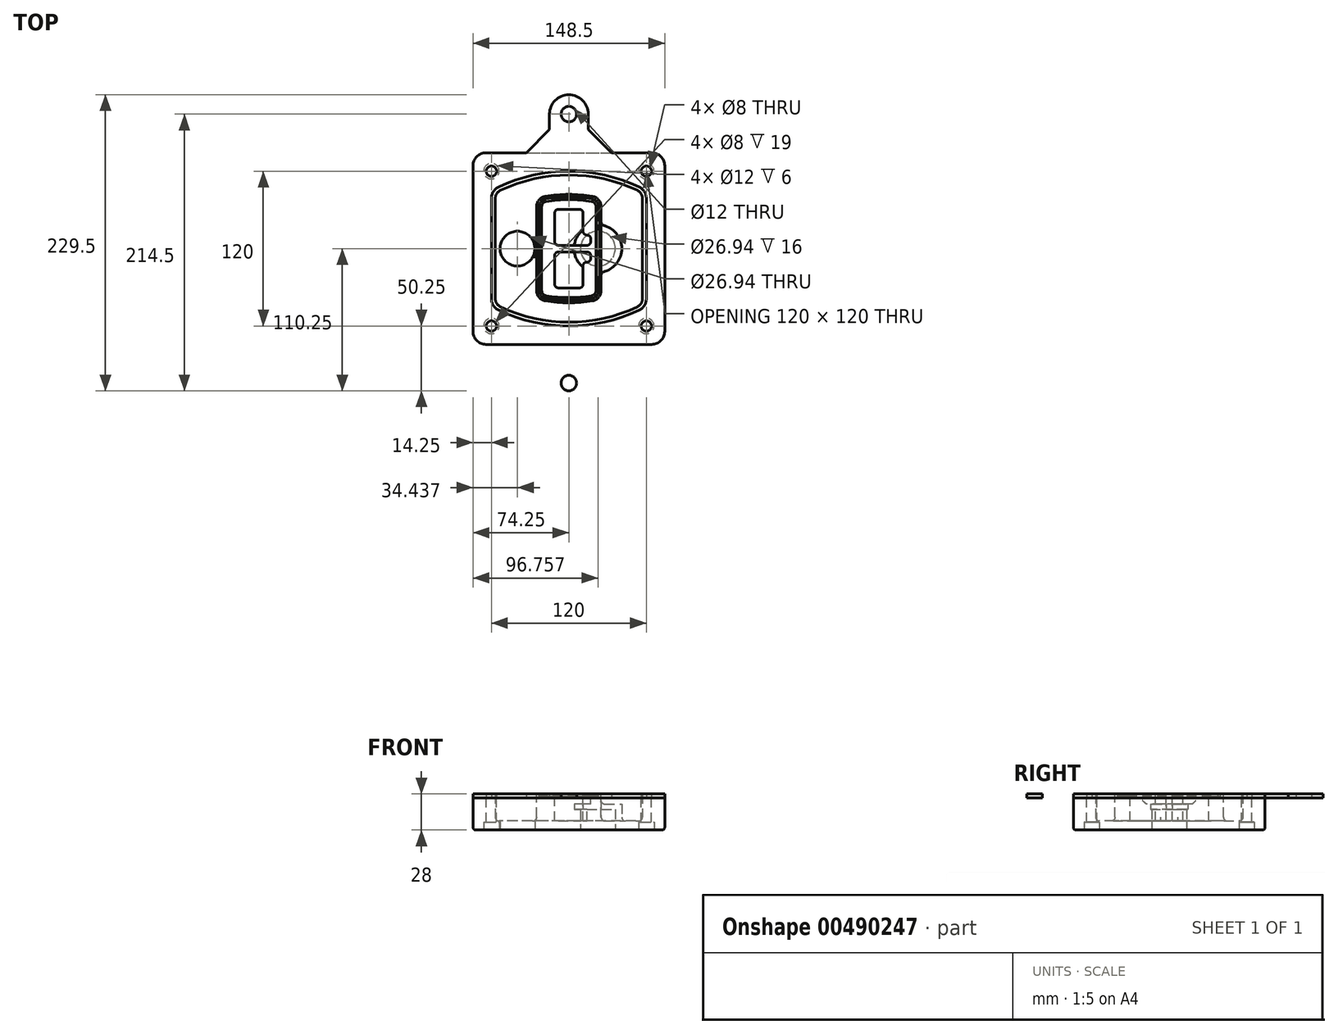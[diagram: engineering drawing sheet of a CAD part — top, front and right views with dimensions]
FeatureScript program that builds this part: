
annotation { "Feature Type Name" : "Feature", "Feature Type Description" : "" }
export const myFeature = defineFeature(function(context is Context, id is Id, definition is map)
    precondition{}
    {
        {
            var Q0;
            Q0=qCreatedBy(makeId("Top.planeOp"),FACE);
            var sketch = newSketch(context, id + "F0", { "sketchPlane" : qUnion([Q0])});
            skPoint(sketch, "E0.rect.middle", {"position": v(0, 0) * mm});
            skLineSegment(sketch, "E1.bottom", {"start": v(-64.25, -74.25) * mm, "end": v(64.25, -74.25) * mm});
            skLineSegment(sketch, "E1.top", {"start": v(-64.25, 74.25) * mm, "end": v(64.25, 74.25) * mm});
            skLineSegment(sketch, "E1.left", {"start": v(-74.25, -64.25) * mm, "end": v(-74.25, 64.25) * mm});
            skLineSegment(sketch, "E1.right", {"start": v(74.25, -64.25) * mm, "end": v(74.25, 64.25) * mm});
            skLineSegment(sketch, "E2", {"start": v(-74.25, 74.25) * mm, "end": v(74.25, -74.25) * mm, "construction": true});
            skLineSegment(sketch, "E3", {"start": v(74.25, 74.25) * mm, "end": v(-74.25, -74.25) * mm, "construction": true});
            skCircle(sketch, "E4", {"center": v(-60, 60) * mm, "radius": 4 * mm});
            skCircle(sketch, "E5", {"center": v(60, 60) * mm, "radius": 4 * mm});
            skCircle(sketch, "E6", {"center": v(60, -60) * mm, "radius": 4 * mm});
            skCircle(sketch, "E7", {"center": v(-60, -60) * mm, "radius": 4 * mm});
            skLineSegment(sketch, "E8", {"start": v(-60, 60) * mm, "end": v(60, 60) * mm, "construction": true});
            skLineSegment(sketch, "E9", {"start": v(60, 60) * mm, "end": v(60, -60) * mm, "construction": true});
            skLineSegment(sketch, "E10", {"start": v(60, -60) * mm, "end": v(-60, -60) * mm, "construction": true});
            skLineSegment(sketch, "E11", {"start": v(-60, -60) * mm, "end": v(-60, 60) * mm, "construction": true});
            skLineSegment(sketch, "E12", {"start": v(-60, 38.83) * mm, "end": v(-60, -38.83) * mm});
            skLineSegment(sketch, "E13", {"start": v(60, 38.83) * mm, "end": v(60, -38.83) * mm});
            skArc(sketch, "E14", {"start": v(54.26, 47.88) * mm, "mid": v(0, 60) * mm, "end": v(-54.26, 47.88) * mm});
            skArc(sketch, "E15", {"start": v(-54.26, -47.88) * mm, "mid": v(0, -60) * mm, "end": v(54.26, -47.88) * mm});
            skLineSegment(sketch, "E16", {"start": v(-60, 0) * mm, "end": v(60, 0) * mm, "construction": true});
            skPoint(sketch, "E17.visualSharp", {"position": v(-60, -45) * mm});
            skArc(sketch, "E17.filletArc", {"start": v(-60, -38.83) * mm, "mid": v(-58.44, -44.2) * mm, "end": v(-54.26, -47.88) * mm});
            skPoint(sketch, "E18.visualSharp", {"position": v(-60, 45) * mm});
            skArc(sketch, "E18.filletArc", {"start": v(-54.26, 47.88) * mm, "mid": v(-58.44, 44.2) * mm, "end": v(-60, 38.83) * mm});
            skPoint(sketch, "E19.visualSharp", {"position": v(60, 45) * mm});
            skArc(sketch, "E19.filletArc", {"start": v(60, 38.83) * mm, "mid": v(58.44, 44.2) * mm, "end": v(54.26, 47.88) * mm});
            skPoint(sketch, "E20.visualSharp", {"position": v(60, -45) * mm});
            skArc(sketch, "E20.filletArc", {"start": v(54.26, -47.88) * mm, "mid": v(58.44, -44.2) * mm, "end": v(60, -38.83) * mm});
            skPoint(sketch, "E21.visualSharp", {"position": v(-74.25, 74.25) * mm});
            skArc(sketch, "E21.filletArc", {"start": v(-64.25, 74.25) * mm, "mid": v(-71.32, 71.32) * mm, "end": v(-74.25, 64.25) * mm});
            skPoint(sketch, "E22.visualSharp", {"position": v(74.25, 74.25) * mm});
            skArc(sketch, "E22.filletArc", {"start": v(74.25, 64.25) * mm, "mid": v(71.32, 71.32) * mm, "end": v(64.25, 74.25) * mm});
            skPoint(sketch, "E23.visualSharp", {"position": v(74.25, -74.25) * mm});
            skArc(sketch, "E23.filletArc", {"start": v(64.25, -74.25) * mm, "mid": v(71.32, -71.32) * mm, "end": v(74.25, -64.25) * mm});
            skPoint(sketch, "E24.visualSharp", {"position": v(-74.25, -74.25) * mm});
            skArc(sketch, "E24.filletArc", {"start": v(-74.25, -64.25) * mm, "mid": v(-71.32, -71.32) * mm, "end": v(-64.25, -74.25) * mm});
            skArc(sketch, "E25.0", {"start": v(57, 38.83) * mm, "mid": v(55.9, 42.58) * mm, "end": v(52.98, 45.17) * mm});
            skLineSegment(sketch, "E25.1", {"start": v(57, 38.83) * mm, "end": v(57, -38.83) * mm});
            skArc(sketch, "E25.2", {"start": v(52.98, -45.17) * mm, "mid": v(55.9, -42.58) * mm, "end": v(57, -38.83) * mm});
            skArc(sketch, "E25.3", {"start": v(-52.98, -45.17) * mm, "mid": v(0, -57) * mm, "end": v(52.98, -45.17) * mm});
            skArc(sketch, "E25.4", {"start": v(-57, -38.83) * mm, "mid": v(-55.9, -42.58) * mm, "end": v(-52.98, -45.17) * mm});
            skArc(sketch, "E25.5", {"start": v(52.98, 45.17) * mm, "mid": v(0, 57) * mm, "end": v(-52.98, 45.17) * mm});
            skLineSegment(sketch, "E25.6", {"start": v(-57, 38.83) * mm, "end": v(-57, -38.83) * mm});
            skArc(sketch, "E25.7", {"start": v(-52.98, 45.17) * mm, "mid": v(-55.9, 42.58) * mm, "end": v(-57, 38.83) * mm});
            skArc(sketch, "E26.0", {"start": v(-55.96, 51.5) * mm, "mid": v(-61.82, 46.33) * mm, "end": v(-64, 38.83) * mm});
            skArc(sketch, "E26.1", {"start": v(55.96, 51.5) * mm, "mid": v(0, 64) * mm, "end": v(-55.96, 51.5) * mm});
            skArc(sketch, "E26.2", {"start": v(64, 38.83) * mm, "mid": v(61.82, 46.33) * mm, "end": v(55.96, 51.5) * mm});
            skLineSegment(sketch, "E26.3", {"start": v(64, 38.83) * mm, "end": v(64, -38.83) * mm});
            skArc(sketch, "E26.4", {"start": v(55.96, -51.5) * mm, "mid": v(61.82, -46.33) * mm, "end": v(64, -38.83) * mm});
            skLineSegment(sketch, "E26.5", {"start": v(-64, 38.83) * mm, "end": v(-64, -38.83) * mm});
            skArc(sketch, "E26.6", {"start": v(-55.96, -51.5) * mm, "mid": v(0, -64) * mm, "end": v(55.96, -51.5) * mm});
            skArc(sketch, "E26.7", {"start": v(-64, -38.83) * mm, "mid": v(-61.82, -46.33) * mm, "end": v(-55.96, -51.5) * mm});
            skSolve(sketch);
        }
        {
            var Q0;
            Q0=makeQuery(id+"F0.imprint","IMPRINT",FACE,{"disambiguationData":[TD([[makeQuery(id+"F0.imprint","IMPRINT",EDGE,{"derivedFrom":sQuery(id+"F0.wireOp",EDGE,"E1.bottom")}),1.0]])]});
            var Q1;
            Q1=makeQuery(id+"F0.imprint","IMPRINT",FACE,{"disambiguationData":[TD([[makeQuery(id+"F0.imprint","IMPRINT",EDGE,{"derivedFrom":sQuery(id+"F0.wireOp",EDGE,"E12")}),1.0]])]});
            var Q2;
            Q2=makeQuery(id+"F0.imprint","IMPRINT",FACE,{"disambiguationData":[TD([[makeQuery(id+"F0.imprint","IMPRINT",EDGE,{"derivedFrom":sQuery(id+"F0.wireOp",EDGE,"E25.0")}),1.0]])]});
            var Q3;
            Q3=makeQuery(id+"F0.imprint","IMPRINT",FACE,{"disambiguationData":[TD([[makeQuery(id+"F0.imprint","IMPRINT",EDGE,{"derivedFrom":sQuery(id+"F0.wireOp",EDGE,"E12")}),-1.0]])]});
            extrude(context, id + "F1", {"entities" : qUnion([Q0, Q1, Q2, Q3]), "oppositeDirection" : true, "depth" : 25 * mm});
        }
        {
            var Q0;
            Q0=makeQuery(id+"F0.imprint","IMPRINT",FACE,{"disambiguationData":[TD([[makeQuery(id+"F0.imprint","IMPRINT",EDGE,{"derivedFrom":sQuery(id+"F0.wireOp",EDGE,"E12")}),1.0]])]});
            extrude(context, id + "F2", {"entities" : qUnion([Q0]), "operationType" : NewBodyOperationType.ADD, "depth" : 3 * mm});
        }
        {
            var Q0;
            Q0=makeQuery(id+"F0.imprint","IMPRINT",FACE,{"disambiguationData":[TD([[makeQuery(id+"F0.imprint","IMPRINT",EDGE,{"derivedFrom":sQuery(id+"F0.wireOp",EDGE,"E25.0")}),1.0]])]});
            extrude(context, id + "F3", {"entities" : qUnion([Q0]), "operationType" : NewBodyOperationType.REMOVE, "oppositeDirection" : true, "depth" : 18 * mm});
        }
        {
            var Q0;
            Q0=makeQuery(id+"F2.opExtrude","CAP_FACE",FACE,{"disambiguationData":[OSD([sQuery(id+"F0.wireOp",EDGE,"E12"),sQuery(id+"F0.wireOp",EDGE,"E13"),sQuery(id+"F0.wireOp",EDGE,"E14"),sQuery(id+"F0.wireOp",EDGE,"E15"),sQuery(id+"F0.wireOp",EDGE,"E17.filletArc"),sQuery(id+"F0.wireOp",EDGE,"E18.filletArc"),sQuery(id+"F0.wireOp",EDGE,"E19.filletArc"),sQuery(id+"F0.wireOp",EDGE,"E20.filletArc"),sQuery(id+"F0.wireOp",EDGE,"E25.0"),sQuery(id+"F0.wireOp",EDGE,"E25.1"),sQuery(id+"F0.wireOp",EDGE,"E25.2"),sQuery(id+"F0.wireOp",EDGE,"E25.3"),sQuery(id+"F0.wireOp",EDGE,"E25.4"),sQuery(id+"F0.wireOp",EDGE,"E25.5"),sQuery(id+"F0.wireOp",EDGE,"E25.6"),sQuery(id+"F0.wireOp",EDGE,"E25.7")])],"isStart":false});
            var sketch = newSketch(context, id + "F4", { "sketchPlane" : qUnion([Q0])});
            skArc(sketch, "E27.0", {"start": v(-18.34, -40.45) * mm, "mid": v(0, -42) * mm, "end": v(18.34, -40.45) * mm});
            skArc(sketch, "E28.0", {"start": v(18.34, 40.45) * mm, "mid": v(0, 42) * mm, "end": v(-18.34, 40.45) * mm});
            skLineSegment(sketch, "E29", {"start": v(-25, 32.57) * mm, "end": v(-25, -32.57) * mm});
            skLineSegment(sketch, "E30", {"start": v(25, 32.57) * mm, "end": v(25, -32.57) * mm});
            skLineSegment(sketch, "E31", {"start": v(-25, 39.1) * mm, "end": v(25, 39.1) * mm, "construction": true});
            skLineSegment(sketch, "E32", {"start": v(-25, -39.1) * mm, "end": v(25, -39.1) * mm, "construction": true});
            skPoint(sketch, "E33.visualSharp", {"position": v(-25, 39.1) * mm});
            skArc(sketch, "E33.filletArc", {"start": v(-18.34, 40.45) * mm, "mid": v(-23.11, 37.73) * mm, "end": v(-25, 32.57) * mm});
            skPoint(sketch, "E34.visualSharp", {"position": v(25, 39.1) * mm});
            skArc(sketch, "E34.filletArc", {"start": v(25, 32.57) * mm, "mid": v(23.11, 37.73) * mm, "end": v(18.34, 40.45) * mm});
            skPoint(sketch, "E35.visualSharp", {"position": v(25, -39.1) * mm});
            skArc(sketch, "E35.filletArc", {"start": v(18.34, -40.45) * mm, "mid": v(23.11, -37.73) * mm, "end": v(25, -32.57) * mm});
            skPoint(sketch, "E36.visualSharp", {"position": v(-25, -39.1) * mm});
            skArc(sketch, "E36.filletArc", {"start": v(-25, -32.57) * mm, "mid": v(-23.11, -37.73) * mm, "end": v(-18.34, -40.45) * mm});
            skArc(sketch, "E37.0", {"start": v(52.98, 45.17) * mm, "mid": v(0, 57) * mm, "end": v(-52.98, 45.17) * mm});
            skArc(sketch, "E37.1", {"start": v(-52.98, 45.17) * mm, "mid": v(-55.9, 42.58) * mm, "end": v(-57, 38.83) * mm});
            skLineSegment(sketch, "E37.2", {"start": v(-57, 38.83) * mm, "end": v(-57, -38.83) * mm});
            skArc(sketch, "E37.3", {"start": v(-57, -38.83) * mm, "mid": v(-55.9, -42.58) * mm, "end": v(-52.98, -45.17) * mm});
            skArc(sketch, "E37.4", {"start": v(-52.98, -45.17) * mm, "mid": v(0, -57) * mm, "end": v(52.98, -45.17) * mm});
            skArc(sketch, "E37.5", {"start": v(52.98, -45.17) * mm, "mid": v(55.9, -42.58) * mm, "end": v(57, -38.83) * mm});
            skLineSegment(sketch, "E37.6", {"start": v(57, 38.83) * mm, "end": v(57, -38.83) * mm});
            skArc(sketch, "E37.7", {"start": v(57, 38.83) * mm, "mid": v(55.9, 42.58) * mm, "end": v(52.98, 45.17) * mm});
            skLineSegment(sketch, "E38.0", {"start": v(23, 32.57) * mm, "end": v(23, -32.57) * mm});
            skArc(sketch, "E38.1", {"start": v(18, -38.48) * mm, "mid": v(21.58, -36.44) * mm, "end": v(23, -32.57) * mm});
            skArc(sketch, "E38.2", {"start": v(-18, -38.48) * mm, "mid": v(0, -40) * mm, "end": v(18, -38.48) * mm});
            skArc(sketch, "E38.3", {"start": v(-23, -32.57) * mm, "mid": v(-21.58, -36.44) * mm, "end": v(-18, -38.48) * mm});
            skLineSegment(sketch, "E38.4", {"start": v(-23, 32.57) * mm, "end": v(-23, -32.57) * mm});
            skArc(sketch, "E38.5", {"start": v(23, 32.57) * mm, "mid": v(21.58, 36.44) * mm, "end": v(18, 38.48) * mm});
            skArc(sketch, "E38.6", {"start": v(-18, 38.48) * mm, "mid": v(-21.58, 36.44) * mm, "end": v(-23, 32.57) * mm});
            skArc(sketch, "E38.7", {"start": v(18, 38.48) * mm, "mid": v(0, 40) * mm, "end": v(-18, 38.48) * mm});
            skArc(sketch, "E39.0", {"start": v(21, 32.57) * mm, "mid": v(20.06, 35.15) * mm, "end": v(17.67, 36.5) * mm});
            skLineSegment(sketch, "E39.1", {"start": v(21, 32.57) * mm, "end": v(21, -32.57) * mm});
            skArc(sketch, "E39.2", {"start": v(17.67, -36.5) * mm, "mid": v(20.06, -35.15) * mm, "end": v(21, -32.57) * mm});
            skArc(sketch, "E39.3", {"start": v(-17.67, -36.5) * mm, "mid": v(0, -38) * mm, "end": v(17.67, -36.5) * mm});
            skArc(sketch, "E39.4", {"start": v(-21, -32.57) * mm, "mid": v(-20.06, -35.15) * mm, "end": v(-17.67, -36.5) * mm});
            skArc(sketch, "E39.5", {"start": v(17.67, 36.5) * mm, "mid": v(0, 38) * mm, "end": v(-17.67, 36.5) * mm});
            skLineSegment(sketch, "E39.6", {"start": v(-21, 32.57) * mm, "end": v(-21, -32.57) * mm});
            skArc(sketch, "E39.7", {"start": v(-17.67, 36.5) * mm, "mid": v(-20.06, 35.15) * mm, "end": v(-21, 32.57) * mm});
            skLineSegment(sketch, "E40", {"start": v(-25, 0) * mm, "end": v(25, 0) * mm, "construction": true});
            skLineSegment(sketch, "E41", {"start": v(-11, 5.5) * mm, "end": v(-11, 27.5) * mm});
            skLineSegment(sketch, "E42", {"start": v(-8, 30.5) * mm, "end": v(8, 30.5) * mm});
            skLineSegment(sketch, "E43", {"start": v(11, 27.5) * mm, "end": v(11, 13.5) * mm});
            skLineSegment(sketch, "E44", {"start": v(14, 10.5) * mm, "end": v(14, 10.5) * mm});
            skLineSegment(sketch, "E45", {"start": v(17, 7.5) * mm, "end": v(17, 5.5) * mm});
            skLineSegment(sketch, "E46", {"start": v(14, 2.5) * mm, "end": v(-8, 2.5) * mm});
            skPoint(sketch, "E47.visualSharp", {"position": v(-11, 30.5) * mm});
            skArc(sketch, "E47.filletArc", {"start": v(-8, 30.5) * mm, "mid": v(-10.12, 29.62) * mm, "end": v(-11, 27.5) * mm});
            skPoint(sketch, "E48.visualSharp", {"position": v(11, 30.5) * mm});
            skArc(sketch, "E48.filletArc", {"start": v(11, 27.5) * mm, "mid": v(10.12, 29.62) * mm, "end": v(8, 30.5) * mm});
            skPoint(sketch, "E49.visualSharp", {"position": v(11, 10.5) * mm});
            skArc(sketch, "E49.filletArc", {"start": v(11, 13.5) * mm, "mid": v(11.88, 11.38) * mm, "end": v(14, 10.5) * mm});
            skPoint(sketch, "E50.visualSharp", {"position": v(17, 10.5) * mm});
            skArc(sketch, "E50.filletArc", {"start": v(17, 7.5) * mm, "mid": v(16.12, 9.62) * mm, "end": v(14, 10.5) * mm});
            skPoint(sketch, "E51.visualSharp", {"position": v(17, 2.5) * mm});
            skArc(sketch, "E51.filletArc", {"start": v(14, 2.5) * mm, "mid": v(16.12, 3.38) * mm, "end": v(17, 5.5) * mm});
            skPoint(sketch, "E52.visualSharp", {"position": v(-11, 2.5) * mm});
            skArc(sketch, "E52.filletArc", {"start": v(-11, 5.5) * mm, "mid": v(-10.12, 3.38) * mm, "end": v(-8, 2.5) * mm});
            skLineSegment(sketch, "E53.0.MirrorCS", {"start": v(14, -2.5) * mm, "end": v(-8, -2.5) * mm});
            skArc(sketch, "E54.0.MirrorCS", {"start": v(-11, -5.5) * mm, "mid": v(-10.12, -3.38) * mm, "end": v(-8, -2.5) * mm});
            skLineSegment(sketch, "E55.0.MirrorCS", {"start": v(-11, -5.5) * mm, "end": v(-11, -27.5) * mm});
            skArc(sketch, "E56.0.MirrorCS", {"start": v(-8, -30.5) * mm, "mid": v(-10.12, -29.62) * mm, "end": v(-11, -27.5) * mm});
            skLineSegment(sketch, "E57.0.MirrorCS", {"start": v(-8, -30.5) * mm, "end": v(8, -30.5) * mm});
            skArc(sketch, "E58.0.MirrorCS", {"start": v(11, -27.5) * mm, "mid": v(10.12, -29.62) * mm, "end": v(8, -30.5) * mm});
            skLineSegment(sketch, "E59.0.MirrorCS", {"start": v(11, -27.5) * mm, "end": v(11, -13.5) * mm});
            skArc(sketch, "E60.0.MirrorCS", {"start": v(11, -13.5) * mm, "mid": v(11.88, -11.38) * mm, "end": v(14, -10.5) * mm});
            skArc(sketch, "E61.0.MirrorCS", {"start": v(17, -7.5) * mm, "mid": v(16.12, -9.62) * mm, "end": v(14, -10.5) * mm});
            skLineSegment(sketch, "E62.0.MirrorCS", {"start": v(17, -7.5) * mm, "end": v(17, -5.5) * mm});
            skArc(sketch, "E63.0.MirrorCS", {"start": v(14, -2.5) * mm, "mid": v(16.12, -3.38) * mm, "end": v(17, -5.5) * mm});
            skSolve(sketch);
        }
        {
            var Q0;
            Q0=makeQuery(id+"F4.imprint","IMPRINT",FACE,{"disambiguationData":[TD([[makeQuery(id+"F4.imprint","IMPRINT",EDGE,{"derivedFrom":sQuery(id+"F4.wireOp",EDGE,"E27.0")}),1.0]])]});
            var Q1;
            Q1=makeQuery(id+"F4.imprint","IMPRINT",FACE,{"disambiguationData":[TD([[makeQuery(id+"F4.imprint","IMPRINT",EDGE,{"derivedFrom":sQuery(id+"F4.wireOp",EDGE,"E38.0")}),-1.0]])]});
            var Q2;
            Q2=makeQuery(id+"F4.imprint","IMPRINT",FACE,{"disambiguationData":[TD([[makeQuery(id+"F4.imprint","IMPRINT",EDGE,{"derivedFrom":sQuery(id+"F4.wireOp",EDGE,"E39.0")}),1.0]])]});
            extrude(context, id + "F5", {"entities" : qUnion([Q0, Q1, Q2]), "operationType" : NewBodyOperationType.ADD, "endBound" : BoundingType.UP_TO_NEXT, "oppositeDirection" : true, "depth" : 25 * mm});
        }
        {
            var Q0;
            Q0=makeQuery(id+"F4.imprint","IMPRINT",FACE,{"disambiguationData":[TD([[makeQuery(id+"F4.imprint","IMPRINT",EDGE,{"derivedFrom":sQuery(id+"F4.wireOp",EDGE,"E38.0")}),-1.0]])]});
            extrude(context, id + "F6", {"entities" : qUnion([Q0]), "operationType" : NewBodyOperationType.REMOVE, "oppositeDirection" : true, "depth" : 2 * mm});
        }
        {
            var Q0;
            Q0=makeQuery(id+"F1.opExtrude","CAP_FACE",FACE,{"disambiguationData":[OSD([sQuery(id+"F0.wireOp",EDGE,"E1.bottom"),sQuery(id+"F0.wireOp",EDGE,"E1.top"),sQuery(id+"F0.wireOp",EDGE,"E1.left"),sQuery(id+"F0.wireOp",EDGE,"E1.right"),sQuery(id+"F0.wireOp",EDGE,"E4"),sQuery(id+"F0.wireOp",EDGE,"E5"),sQuery(id+"F0.wireOp",EDGE,"E6"),sQuery(id+"F0.wireOp",EDGE,"E7"),sQuery(id+"F0.wireOp",EDGE,"E21.filletArc"),sQuery(id+"F0.wireOp",EDGE,"E22.filletArc"),sQuery(id+"F0.wireOp",EDGE,"E23.filletArc"),sQuery(id+"F0.wireOp",EDGE,"E24.filletArc")])],"isStart":false});
            var sketch = newSketch(context, id + "F7", { "sketchPlane" : qUnion([Q0])});
            skCircle(sketch, "E64", {"center": v(22.5, 0) * mm, "radius": 13.47 * mm});
            skCircle(sketch, "E65", {"center": v(-39.81, 0) * mm, "radius": 13.47 * mm});
            skLineSegment(sketch, "E66", {"start": v(74.25, 0) * mm, "end": v(-74.25, 0) * mm});
            skCircle(sketch, "E67", {"center": v(22.5, 0) * mm, "radius": 18.47 * mm});
            skCircle(sketch, "E68", {"center": v(60, -60) * mm, "radius": 6 * mm});
            skCircle(sketch, "E69", {"center": v(-60, -60) * mm, "radius": 6 * mm});
            skCircle(sketch, "E70", {"center": v(-60, 60) * mm, "radius": 6 * mm});
            skCircle(sketch, "E71", {"center": v(60, 60) * mm, "radius": 6 * mm});
            skSolve(sketch);
        }
        {
            var Q0;
            {var subQ1=sQuery(id+"F7.wireOp",EDGE,"E66");var subQ4=sQuery(id+"F7.wireOp",EDGE,"E64");var subQ6=makeQuery(id+"F7.imprint","INTERSECT",VERTEX,{"disambiguationData":[OD(0.0)],"derivedFrom":[subQ4,subQ1]});Q0=makeQuery(id+"F7.imprint","IMPRINT",FACE,{"disambiguationData":[TD([[makeQuery(id+"F7.imprint","IMPRINT",EDGE,{"disambiguationData":[TD([[subQ6,-1.0]])],"derivedFrom":subQ4}),-1.0]])]});}
            var Q1;
            {var subQ0=sQuery(id+"F7.wireOp",EDGE,"E66");var subQ1=sQuery(id+"F7.wireOp",EDGE,"E64");var subQ3=makeQuery(id+"F7.imprint","INTERSECT",VERTEX,{"disambiguationData":[OD(0.0)],"derivedFrom":[subQ1,subQ0]});Q1=makeQuery(id+"F7.imprint","IMPRINT",FACE,{"disambiguationData":[TD([[makeQuery(id+"F7.imprint","IMPRINT",EDGE,{"disambiguationData":[TD([[subQ3,-1.0]])],"derivedFrom":subQ1}),1.0]])]});}
            var Q2;
            {var subQ0=sQuery(id+"F7.wireOp",EDGE,"E66");var subQ1=sQuery(id+"F7.wireOp",EDGE,"E64");var subQ3=makeQuery(id+"F7.imprint","INTERSECT",VERTEX,{"disambiguationData":[OD(0.0)],"derivedFrom":[subQ1,subQ0]});Q2=makeQuery(id+"F7.imprint","IMPRINT",FACE,{"disambiguationData":[TD([[makeQuery(id+"F7.imprint","IMPRINT",EDGE,{"disambiguationData":[TD([[subQ3,1.0]])],"derivedFrom":subQ1}),1.0]])]});}
            var Q3;
            {var subQ1=sQuery(id+"F7.wireOp",EDGE,"E66");var subQ4=sQuery(id+"F7.wireOp",EDGE,"E64");var subQ6=makeQuery(id+"F7.imprint","INTERSECT",VERTEX,{"disambiguationData":[OD(0.0)],"derivedFrom":[subQ4,subQ1]});Q3=makeQuery(id+"F7.imprint","IMPRINT",FACE,{"disambiguationData":[TD([[makeQuery(id+"F7.imprint","IMPRINT",EDGE,{"disambiguationData":[TD([[subQ6,1.0]])],"derivedFrom":subQ4}),-1.0]])]});}
            extrude(context, id + "F8", {"entities" : qUnion([Q0, Q1, Q2, Q3]), "operationType" : NewBodyOperationType.ADD, "oppositeDirection" : true, "depth" : 20 * mm});
        }
        {
            var Q0;
            {var subQ0=sQuery(id+"F7.wireOp",EDGE,"E66");var subQ1=sQuery(id+"F7.wireOp",EDGE,"E64");var subQ3=makeQuery(id+"F7.imprint","INTERSECT",VERTEX,{"disambiguationData":[OD(0.0)],"derivedFrom":[subQ1,subQ0]});Q0=makeQuery(id+"F7.imprint","IMPRINT",FACE,{"disambiguationData":[TD([[makeQuery(id+"F7.imprint","IMPRINT",EDGE,{"disambiguationData":[TD([[subQ3,-1.0]])],"derivedFrom":subQ1}),1.0]])]});}
            var Q1;
            {var subQ0=sQuery(id+"F7.wireOp",EDGE,"E66");var subQ1=sQuery(id+"F7.wireOp",EDGE,"E64");var subQ3=makeQuery(id+"F7.imprint","INTERSECT",VERTEX,{"disambiguationData":[OD(0.0)],"derivedFrom":[subQ1,subQ0]});Q1=makeQuery(id+"F7.imprint","IMPRINT",FACE,{"disambiguationData":[TD([[makeQuery(id+"F7.imprint","IMPRINT",EDGE,{"disambiguationData":[TD([[subQ3,1.0]])],"derivedFrom":subQ1}),1.0]])]});}
            extrude(context, id + "F9", {"entities" : qUnion([Q0, Q1]), "operationType" : NewBodyOperationType.REMOVE, "oppositeDirection" : true, "depth" : 16 * mm});
        }
        {
            var Q0;
            {var subQ0=sQuery(id+"F7.wireOp",EDGE,"E66");var subQ1=sQuery(id+"F7.wireOp",EDGE,"E65");var subQ3=makeQuery(id+"F7.imprint","INTERSECT",VERTEX,{"disambiguationData":[OD(0.0)],"derivedFrom":[subQ1,subQ0]});Q0=makeQuery(id+"F7.imprint","IMPRINT",FACE,{"disambiguationData":[TD([[makeQuery(id+"F7.imprint","IMPRINT",EDGE,{"disambiguationData":[TD([[subQ3,-1.0]])],"derivedFrom":subQ1}),1.0]])]});}
            var Q1;
            {var subQ0=sQuery(id+"F7.wireOp",EDGE,"E66");var subQ1=sQuery(id+"F7.wireOp",EDGE,"E65");var subQ3=makeQuery(id+"F7.imprint","INTERSECT",VERTEX,{"disambiguationData":[OD(0.0)],"derivedFrom":[subQ1,subQ0]});Q1=makeQuery(id+"F7.imprint","IMPRINT",FACE,{"disambiguationData":[TD([[makeQuery(id+"F7.imprint","IMPRINT",EDGE,{"disambiguationData":[TD([[subQ3,1.0]])],"derivedFrom":subQ1}),1.0]])]});}
            extrude(context, id + "F10", {"entities" : qUnion([Q0, Q1]), "operationType" : NewBodyOperationType.REMOVE, "oppositeDirection" : true, "depth" : 25 * mm});
        }
        {
            var Q0;
            Q0=makeQuery(id+"F7.imprint","IMPRINT",FACE,{"disambiguationData":[TD([[makeQuery(id+"F7.imprint","IMPRINT",EDGE,{"derivedFrom":sQuery(id+"F7.wireOp",EDGE,"E68")}),1.0]])]});
            var Q1;
            Q1=makeQuery(id+"F7.imprint","IMPRINT",FACE,{"disambiguationData":[TD([[makeQuery(id+"F7.imprint","IMPRINT",EDGE,{"derivedFrom":makeQuery(id+"F1.opExtrude","CAP_EDGE",EDGE,{"disambiguationData":[OSD([sQuery(id+"F0.wireOp",EDGE,"E5")])],"isStart":false})}),-1.0]])]});
            var Q2;
            Q2=makeQuery(id+"F7.imprint","IMPRINT",FACE,{"disambiguationData":[TD([[makeQuery(id+"F7.imprint","IMPRINT",EDGE,{"derivedFrom":sQuery(id+"F7.wireOp",EDGE,"E69")}),1.0]])]});
            var Q3;
            Q3=makeQuery(id+"F7.imprint","IMPRINT",FACE,{"disambiguationData":[TD([[makeQuery(id+"F7.imprint","IMPRINT",EDGE,{"derivedFrom":makeQuery(id+"F1.opExtrude","CAP_EDGE",EDGE,{"disambiguationData":[OSD([sQuery(id+"F0.wireOp",EDGE,"E4")])],"isStart":false})}),-1.0]])]});
            var Q4;
            Q4=makeQuery(id+"F7.imprint","IMPRINT",FACE,{"disambiguationData":[TD([[makeQuery(id+"F7.imprint","IMPRINT",EDGE,{"derivedFrom":sQuery(id+"F7.wireOp",EDGE,"E70")}),1.0]])]});
            var Q5;
            Q5=makeQuery(id+"F7.imprint","IMPRINT",FACE,{"disambiguationData":[TD([[makeQuery(id+"F7.imprint","IMPRINT",EDGE,{"derivedFrom":makeQuery(id+"F1.opExtrude","CAP_EDGE",EDGE,{"disambiguationData":[OSD([sQuery(id+"F0.wireOp",EDGE,"E7")])],"isStart":false})}),-1.0]])]});
            var Q6;
            Q6=makeQuery(id+"F7.imprint","IMPRINT",FACE,{"disambiguationData":[TD([[makeQuery(id+"F7.imprint","IMPRINT",EDGE,{"derivedFrom":sQuery(id+"F7.wireOp",EDGE,"E71")}),1.0]])]});
            var Q7;
            Q7=makeQuery(id+"F7.imprint","IMPRINT",FACE,{"disambiguationData":[TD([[makeQuery(id+"F7.imprint","IMPRINT",EDGE,{"derivedFrom":makeQuery(id+"F1.opExtrude","CAP_EDGE",EDGE,{"disambiguationData":[OSD([sQuery(id+"F0.wireOp",EDGE,"E6")])],"isStart":false})}),-1.0]])]});
            extrude(context, id + "F11", {"entities" : qUnion([Q0, Q1, Q2, Q3, Q4, Q5, Q6, Q7]), "operationType" : NewBodyOperationType.REMOVE, "oppositeDirection" : true, "depth" : 6 * mm});
        }
        {
            var Q0;
            Q0=makeQuery(id+"F9.boolean.opBoolean","COPY",FACE,{"derivedFrom":makeQuery(id+"F9.opExtrude","CAP_FACE",FACE,{"disambiguationData":[OSD([sQuery(id+"F7.wireOp",EDGE,"E64")])],"isStart":false})});
            var sketch = newSketch(context, id + "F12", { "sketchPlane" : qUnion([Q0])});
            skArc(sketch, "E72.0", {"start": v(11, 14.45) * mm, "mid": v(6.45, 9.13) * mm, "end": v(4.2, 2.5) * mm});
            skArc(sketch, "E72.1", {"start": v(4.2, -2.5) * mm, "mid": v(6.45, -9.13) * mm, "end": v(11, -14.45) * mm});
            skLineSegment(sketch, "E73", {"start": v(4.2, -2.5) * mm, "end": v(14, -2.5) * mm});
            skLineSegment(sketch, "E74.0", {"start": v(14, 2.5) * mm, "end": v(4.2, 2.5) * mm});
            skArc(sketch, "E74.1", {"start": v(14, 2.5) * mm, "mid": v(16.12, 3.38) * mm, "end": v(17, 5.5) * mm});
            skLineSegment(sketch, "E74.2", {"start": v(17, 7.5) * mm, "end": v(17, 5.5) * mm});
            skArc(sketch, "E74.3", {"start": v(17, 7.5) * mm, "mid": v(16.12, 9.62) * mm, "end": v(14, 10.5) * mm});
            skArc(sketch, "E74.4", {"start": v(11, 13.5) * mm, "mid": v(11.88, 11.38) * mm, "end": v(14, 10.5) * mm});
            skLineSegment(sketch, "E74.5", {"start": v(11, 14.45) * mm, "end": v(11, 13.5) * mm});
            skLineSegment(sketch, "E74.7", {"start": v(14, -2.5) * mm, "end": v(4.2, -2.5) * mm});
            skArc(sketch, "E74.8", {"start": v(14, -2.5) * mm, "mid": v(16.12, -3.38) * mm, "end": v(17, -5.5) * mm});
            skLineSegment(sketch, "E74.9", {"start": v(17, -7.5) * mm, "end": v(17, -5.5) * mm});
            skArc(sketch, "E74.10", {"start": v(17, -7.5) * mm, "mid": v(16.12, -9.62) * mm, "end": v(14, -10.5) * mm});
            skArc(sketch, "E74.11", {"start": v(11, -13.5) * mm, "mid": v(11.88, -11.38) * mm, "end": v(14, -10.5) * mm});
            skLineSegment(sketch, "E74.12", {"start": v(11, -14.45) * mm, "end": v(11, -13.5) * mm});
            skPoint(sketch, "E75.orphan", {"position": v(11, -27.5) * mm});
            skPoint(sketch, "E76.orphan", {"position": v(-8, -2.5) * mm});
            skPoint(sketch, "E77.orphan", {"position": v(-8, 2.5) * mm});
            skPoint(sketch, "E78.orphan", {"position": v(11, 27.5) * mm});
            skSolve(sketch);
        }
        {
            var Q0;
            {var subQ7=sQuery(id+"F12.wireOp",EDGE,"E72.0");var subQ14=sQuery(id+"F12.wireOp",EDGE,"E72.1");var subQ16=sQuery(id+"F12.wireOp",EDGE,"E74.1");var subQ18=sQuery(id+"F12.wireOp",EDGE,"E74.8");Q0=qUnion([makeQuery(id+"F12.imprint","IMPRINT",FACE,{"disambiguationData":[TD([[makeQuery(id+"F12.imprint","IMPRINT",EDGE,{"derivedFrom":subQ7}),1.0]])]}),makeQuery(id+"F12.imprint","IMPRINT",FACE,{"disambiguationData":[TD([[makeQuery(id+"F12.imprint","IMPRINT",EDGE,{"derivedFrom":subQ14}),1.0]])]}),makeQuery(id+"F12.imprint","IMPRINT",FACE,{"disambiguationData":[TD([[makeQuery(id+"F12.imprint","IMPRINT",EDGE,{"derivedFrom":subQ16}),1.0]])]}),makeQuery(id+"F12.imprint","IMPRINT",FACE,{"disambiguationData":[TD([[makeQuery(id+"F12.imprint","IMPRINT",EDGE,{"derivedFrom":subQ18}),-1.0]])]})]);}
            var Q1;
            Q1=makeQuery(id+"F5.boolean.opBoolean","SPLIT",FACE,{"disambiguationData":[TD([makeQuery(id+"F5.opExtrude","SWEPT_FACE",FACE,{"disambiguationData":[OSD([sQuery(id+"F4.wireOp",EDGE,"E41")])]})])],"derivedFrom":makeQuery(id+"F3.boolean.opBoolean","COPY",FACE,{"derivedFrom":makeQuery(id+"F3.opExtrude","CAP_FACE",FACE,{"disambiguationData":[OSD([sQuery(id+"F0.wireOp",EDGE,"E25.0"),sQuery(id+"F0.wireOp",EDGE,"E25.1"),sQuery(id+"F0.wireOp",EDGE,"E25.2"),sQuery(id+"F0.wireOp",EDGE,"E25.3"),sQuery(id+"F0.wireOp",EDGE,"E25.4"),sQuery(id+"F0.wireOp",EDGE,"E25.5"),sQuery(id+"F0.wireOp",EDGE,"E25.6"),sQuery(id+"F0.wireOp",EDGE,"E25.7")])],"isStart":false})})});
            extrude(context, id + "F13", {"entities" : qUnion([Q0]), "operationType" : NewBodyOperationType.REMOVE, "endBound" : BoundingType.UP_TO_SURFACE, "endBoundEntityFace" : qUnion([Q1]), "depth" : 25 * mm});
        }
        {
            var Q0;
            Q0=makeQuery(id+"F3.boolean.opBoolean","COPY",EDGE,{"derivedFrom":makeQuery(id+"F3.opExtrude","CAP_EDGE",EDGE,{"disambiguationData":[OSD([sQuery(id+"F0.wireOp",EDGE,"E25.6")])],"isStart":false})});
            var Q1;
            Q1=makeQuery(id+"F8.boolean.opBoolean","INTERSECT",EDGE,{"derivedFrom":[makeQuery(id+"F5.opExtrude","SWEPT_FACE",FACE,{"disambiguationData":[OSD([sQuery(id+"F4.wireOp",EDGE,"E30")])]}),makeQuery(id+"F8.opExtrude","CAP_FACE",FACE,{"disambiguationData":[OSD([sQuery(id+"F7.wireOp",EDGE,"E67")])],"isStart":false})]});
            var Q2;
            Q2=makeQuery(id+"F8.boolean.opBoolean","INTERSECT",EDGE,{"disambiguationData":[OD(1.0)],"derivedFrom":[makeQuery(id+"F5.opExtrude","SWEPT_FACE",FACE,{"disambiguationData":[OSD([sQuery(id+"F4.wireOp",EDGE,"E30")])]}),makeQuery(id+"F8.opExtrude","SWEPT_FACE",FACE,{"disambiguationData":[OSD([sQuery(id+"F7.wireOp",EDGE,"E67")])]})]});
            var Q3;
            {var subQ0=sQuery(id+"F4.wireOp",EDGE,"E30");Q3=makeQuery(id+"F8.boolean.opBoolean","SPLIT",EDGE,{"disambiguationData":[TD([makeQuery(id+"F5.opExtrude","SWEPT_FACE",FACE,{"disambiguationData":[OSD([sQuery(id+"F4.wireOp",EDGE,"E35.filletArc")])]})])],"derivedFrom":makeQuery(id+"F5.opExtrude","CAP_EDGE",EDGE,{"disambiguationData":[OSD([subQ0])],"isStart":false})});}
            var Q4;
            {var subQ0=sQuery(id+"F0.wireOp",EDGE,"E25.7");var subQ1=sQuery(id+"F0.wireOp",EDGE,"E25.1");var subQ2=sQuery(id+"F0.wireOp",EDGE,"E25.6");var subQ3=sQuery(id+"F0.wireOp",EDGE,"E25.5");var subQ4=sQuery(id+"F0.wireOp",EDGE,"E25.4");var subQ5=sQuery(id+"F0.wireOp",EDGE,"E25.0");var subQ6=sQuery(id+"F0.wireOp",EDGE,"E25.2");var subQ7=sQuery(id+"F0.wireOp",EDGE,"E25.3");Q4=makeQuery(id+"F8.boolean.opBoolean","INTERSECT",EDGE,{"derivedFrom":[makeQuery(id+"F5.boolean.opBoolean","SPLIT",FACE,{"disambiguationData":[TD([makeQuery(id+"F2.opExtrude","SWEPT_FACE",FACE,{"disambiguationData":[OSD([subQ5])]})])],"derivedFrom":makeQuery(id+"F3.boolean.opBoolean","COPY",FACE,{"derivedFrom":makeQuery(id+"F3.opExtrude","CAP_FACE",FACE,{"disambiguationData":[OSD([subQ5,subQ1,subQ6,subQ7,subQ4,subQ3,subQ2,subQ0])],"isStart":false})})}),makeQuery(id+"F8.opExtrude","SWEPT_FACE",FACE,{"disambiguationData":[OSD([sQuery(id+"F7.wireOp",EDGE,"E67")])]})]});}
            var Q5;
            Q5=makeQuery(id+"F8.boolean.opBoolean","INTERSECT",EDGE,{"disambiguationData":[OD(0.0)],"derivedFrom":[makeQuery(id+"F5.opExtrude","SWEPT_FACE",FACE,{"disambiguationData":[OSD([sQuery(id+"F4.wireOp",EDGE,"E30")])]}),makeQuery(id+"F8.opExtrude","SWEPT_FACE",FACE,{"disambiguationData":[OSD([sQuery(id+"F7.wireOp",EDGE,"E67")])]})]});
            fillet(context, id + "F14", {"entities" : qUnion([Q0, Q1, Q2, Q3, Q4, Q5]), "radius" : 3 * mm, "tangentPropagation" : true, "allowEdgeOverflow" : false});
        }
        {
            var Q0;
            Q0=makeQuery(id+"F1.opExtrude","CAP_EDGE",EDGE,{"disambiguationData":[OSD([sQuery(id+"F0.wireOp",EDGE,"E1.bottom")])],"isStart":false});
            fillet(context, id + "F15", {"entities" : qUnion([Q0]), "radius" : 2 * mm, "tangentPropagation" : true, "allowEdgeOverflow" : false});
        }
        {
            var Q0;
            {var subQ0=sQuery(id+"F0.wireOp",EDGE,"E21.filletArc");var subQ1=sQuery(id+"F0.wireOp",EDGE,"E7");var subQ2=sQuery(id+"F0.wireOp",EDGE,"E6");var subQ3=sQuery(id+"F0.wireOp",EDGE,"E5");var subQ4=sQuery(id+"F0.wireOp",EDGE,"E4");var subQ5=sQuery(id+"F0.wireOp",EDGE,"E22.filletArc");var subQ6=sQuery(id+"F0.wireOp",EDGE,"E1.bottom");var subQ7=sQuery(id+"F0.wireOp",EDGE,"E1.right");var subQ8=sQuery(id+"F0.wireOp",EDGE,"E1.top");var subQ9=sQuery(id+"F0.wireOp",EDGE,"E1.left");var subQ10=sQuery(id+"F0.wireOp",EDGE,"E23.filletArc");var subQ11=sQuery(id+"F0.wireOp",EDGE,"E24.filletArc");Q0=makeQuery(id+"F2.boolean.opBoolean","SPLIT",FACE,{"disambiguationData":[TD([makeQuery(id+"F1.opExtrude","SWEPT_FACE",FACE,{"disambiguationData":[OSD([subQ6])]})])],"derivedFrom":makeQuery(id+"F1.opExtrude","CAP_FACE",FACE,{"disambiguationData":[OSD([subQ6,subQ8,subQ9,subQ7,subQ4,subQ3,subQ2,subQ1,subQ0,subQ5,subQ10,subQ11])],"isStart":true})});}
            var sketch = newSketch(context, id + "F16", { "sketchPlane" : qUnion([Q0])});
            skLineSegment(sketch, "E79", {"start": v(0, 74.25) * mm, "end": v(0, 104.25) * mm, "construction": true});
            skArc(sketch, "E80", {"start": v(15, 104.25) * mm, "mid": v(0, 119.25) * mm, "end": v(-15, 104.25) * mm});
            skLineSegment(sketch, "E81", {"start": v(15, 104.25) * mm, "end": v(15, 92.25) * mm});
            skLineSegment(sketch, "E82", {"start": v(-15, 104.25) * mm, "end": v(-15, 92.25) * mm});
            skLineSegment(sketch, "E83", {"start": v(15, 92.25) * mm, "end": v(33, 74.25) * mm});
            skLineSegment(sketch, "E84", {"start": v(-15, 92.25) * mm, "end": v(-33, 74.25) * mm});
            skCircle(sketch, "E85", {"center": v(0, 104.25) * mm, "radius": 6 * mm});
            skLineSegment(sketch, "E86", {"start": v(-74.25, 0) * mm, "end": v(74.25, 0) * mm, "construction": true});
            skLineSegment(sketch, "E87.MirrorCS", {"start": v(0, -74.25) * mm, "end": v(0, -104.25) * mm, "construction": true});
            skArc(sketch, "E88.MirrorCS", {"start": v(15, -104.25) * mm, "mid": v(0, -119.25) * mm, "end": v(-15, -104.25) * mm});
            skLineSegment(sketch, "E89.MirrorCS", {"start": v(15, -104.25) * mm, "end": v(15, -92.25) * mm});
            skLineSegment(sketch, "E90.MirrorCS", {"start": v(-15, -104.25) * mm, "end": v(-15, -92.25) * mm});
            skLineSegment(sketch, "E91.MirrorCS", {"start": v(15, -92.25) * mm, "end": v(33, -74.25) * mm});
            skLineSegment(sketch, "E92.MirrorCS", {"start": v(-15, -92.25) * mm, "end": v(-33, -74.25) * mm});
            skCircle(sketch, "E93.MirrorC", {"center": v(0, -104.25) * mm, "radius": 6 * mm});
            skSolve(sketch);
        }
        {
            var Q0;
            Q0=makeQuery(id+"F16.imprint","IMPRINT",FACE,{"disambiguationData":[TD([[makeQuery(id+"F16.imprint","IMPRINT",EDGE,{"derivedFrom":sQuery(id+"F16.wireOp",EDGE,"E80")}),1.0]])]});
            var Q1;
            Q1=makeQuery(id+"F16.imprint","IMPRINT",FACE,{"disambiguationData":[TD([[makeQuery(id+"F16.imprint","IMPRINT",EDGE,{"derivedFrom":makeQuery(id+"F1.opExtrude","CAP_EDGE",EDGE,{"disambiguationData":[OSD([sQuery(id+"F0.wireOp",EDGE,"E1.left")])],"isStart":true})}),-1.0]])]});
            var Q2;
            Q2=makeQuery(id+"F16.imprint","IMPRINT",FACE,{"disambiguationData":[TD([[makeQuery(id+"F16.imprint","IMPRINT",EDGE,{"derivedFrom":sQuery(id+"F16.wireOp",EDGE,"E93.MirrorC")}),1.0]])]});
            var Q3;
            Q3=makeQuery(id+"F2.opExtrude","CAP_FACE",FACE,{"disambiguationData":[OSD([sQuery(id+"F0.wireOp",EDGE,"E12"),sQuery(id+"F0.wireOp",EDGE,"E13"),sQuery(id+"F0.wireOp",EDGE,"E14"),sQuery(id+"F0.wireOp",EDGE,"E15"),sQuery(id+"F0.wireOp",EDGE,"E17.filletArc"),sQuery(id+"F0.wireOp",EDGE,"E18.filletArc"),sQuery(id+"F0.wireOp",EDGE,"E19.filletArc"),sQuery(id+"F0.wireOp",EDGE,"E20.filletArc"),sQuery(id+"F0.wireOp",EDGE,"E25.0"),sQuery(id+"F0.wireOp",EDGE,"E25.1"),sQuery(id+"F0.wireOp",EDGE,"E25.2"),sQuery(id+"F0.wireOp",EDGE,"E25.3"),sQuery(id+"F0.wireOp",EDGE,"E25.4"),sQuery(id+"F0.wireOp",EDGE,"E25.5"),sQuery(id+"F0.wireOp",EDGE,"E25.6"),sQuery(id+"F0.wireOp",EDGE,"E25.7")])],"isStart":false});
            extrude(context, id + "F17", {"entities" : qUnion([Q0, Q1, Q2]), "endBound" : BoundingType.UP_TO_SURFACE, "endBoundEntityFace" : qUnion([Q3]), "depth" : 25 * mm});
        }
    });
